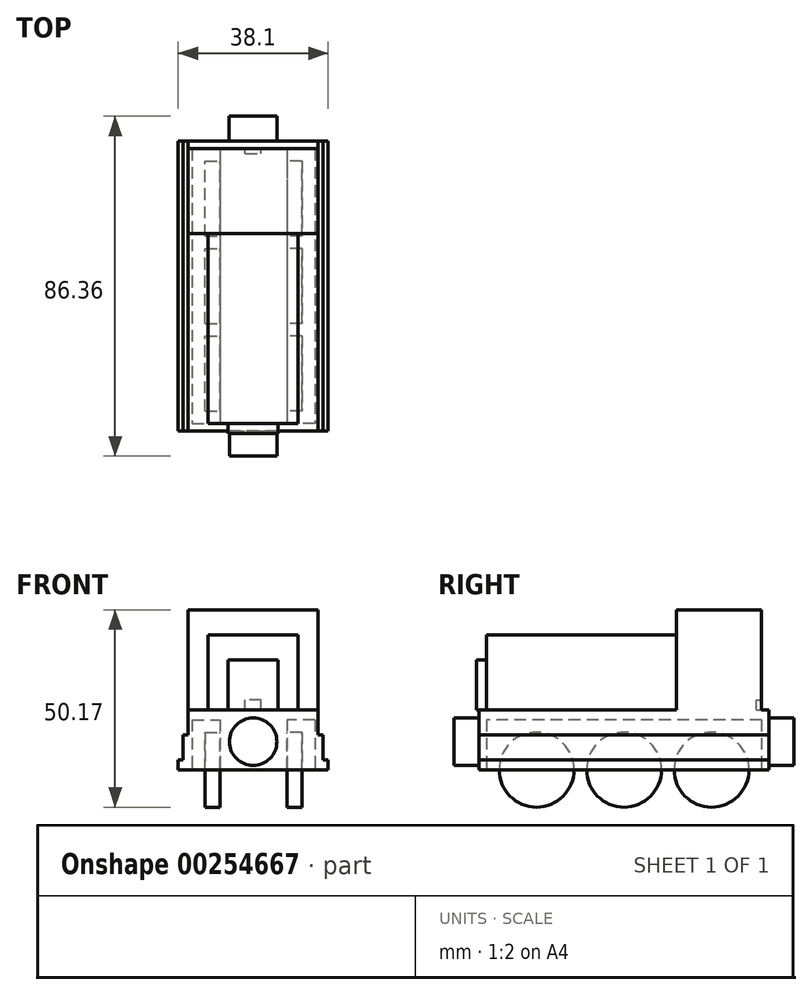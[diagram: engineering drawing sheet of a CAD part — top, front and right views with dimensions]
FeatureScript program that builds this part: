
annotation { "Feature Type Name" : "Feature", "Feature Type Description" : "" }
export const myFeature = defineFeature(function(context is Context, id is Id, definition is map)
    precondition{}
    {
        {
            var Q0;
            Q0=qCreatedBy(makeId("Front.planeOp"),FACE);
            var sketch = newSketch(context, id + "F0", { "sketchPlane" : qUnion([Q0])});
            skLineSegment(sketch, "E0.bottom", {"start": v(-16.51, 12.7) * mm, "end": v(16.51, 12.7) * mm});
            skLineSegment(sketch, "E0.top", {"start": v(-16.51, -12.7) * mm, "end": v(16.51, -12.7) * mm});
            skLineSegment(sketch, "E0.left", {"start": v(-16.51, 12.7) * mm, "end": v(-16.51, -12.7) * mm});
            skLineSegment(sketch, "E0.right", {"start": v(16.51, 12.7) * mm, "end": v(16.51, -12.7) * mm});
            skPoint(sketch, "E0.middle", {"position": v(0, 0) * mm});
            skSolve(sketch);
        }
        {
            var Q0;
            Q0 = qSketchRegion(id + "F0", true);
            extrude(context, id + "F1", {"entities" : qUnion([Q0]), "endBound" : BoundingType.SYMMETRIC, "depth" : 21.59 * mm});
        }
        {
            var Q0;
            Q0=makeQuery(id+"F1.opExtrude","CAP_FACE",FACE,{"disambiguationData":[OSD([sQuery(id+"F0.wireOp",EDGE,"E0.bottom"),sQuery(id+"F0.wireOp",EDGE,"E0.top"),sQuery(id+"F0.wireOp",EDGE,"E0.left"),sQuery(id+"F0.wireOp",EDGE,"E0.right")])],"isStart":false});
            var sketch = newSketch(context, id + "F2", { "sketchPlane" : qUnion([Q0])});
            skLineSegment(sketch, "E1.bottom", {"start": v(-11.43, 6.35) * mm, "end": v(11.43, 6.35) * mm});
            skLineSegment(sketch, "E1.top", {"start": v(-11.43, -12.7) * mm, "end": v(11.43, -12.7) * mm});
            skLineSegment(sketch, "E1.left", {"start": v(-11.43, 6.35) * mm, "end": v(-11.43, -12.7) * mm});
            skLineSegment(sketch, "E1.right", {"start": v(11.43, 6.35) * mm, "end": v(11.43, -12.7) * mm});
            skPoint(sketch, "E2", {"position": v(0, -12.7) * mm});
            skPoint(sketch, "E3", {"position": v(67.06, 31.88) * mm});
            skSolve(sketch);
        }
        {
            var Q0;
            Q0 = qSketchRegion(id + "F2", true);
            extrude(context, id + "F3", {"entities" : qUnion([Q0]), "operationType" : NewBodyOperationType.ADD, "depth" : 48.26 * mm});
        }
        {
            var Q0;
            Q0=qCreatedBy(makeId("Front.planeOp"),FACE);
            var sketch = newSketch(context, id + "F4", { "sketchPlane" : qUnion([Q0])});
            skLineSegment(sketch, "E4.bottom", {"start": v(-16.5, -12.7) * mm, "end": v(16.51, -12.7) * mm});
            skLineSegment(sketch, "E4.top", {"start": v(-16.5, -27.94) * mm, "end": v(16.51, -27.94) * mm});
            skLineSegment(sketch, "E4.left", {"start": v(-16.5, -12.7) * mm, "end": v(-16.5, -27.94) * mm});
            skLineSegment(sketch, "E4.right", {"start": v(16.51, -12.7) * mm, "end": v(16.51, -27.94) * mm});
            skSolve(sketch);
        }
        {
            var Q0;
            Q0=makeQuery(id+"F4.imprint","IMPRINT",FACE,{"disambiguationData":[TD([[makeQuery(id+"F4.imprint","IMPRINT",EDGE,{"derivedFrom":sQuery(id+"F4.wireOp",EDGE,"E4.bottom")}),-1.0]])]});
            extrude(context, id + "F5", {"entities" : qUnion([Q0]), "operationType" : NewBodyOperationType.ADD, "endBound" : BoundingType.SYMMETRIC, "depth" : 25.4 * mm});
        }
        {
            var Q0;
            Q0=makeQuery(id+"F5.opExtrude","CAP_FACE",FACE,{"disambiguationData":[OSD([sQuery(id+"F4.wireOp",EDGE,"E4.bottom"),sQuery(id+"F4.wireOp",EDGE,"E4.top"),sQuery(id+"F4.wireOp",EDGE,"E4.left"),sQuery(id+"F4.wireOp",EDGE,"E4.right")])],"isStart":false});
            var sketch = newSketch(context, id + "F6", { "sketchPlane" : qUnion([Q0])});
            skLineSegment(sketch, "E5.bottom", {"start": v(-16.5, -12.7) * mm, "end": v(16.51, -12.7) * mm});
            skLineSegment(sketch, "E5.top", {"start": v(-16.5, -27.94) * mm, "end": v(16.51, -27.94) * mm});
            skLineSegment(sketch, "E5.left", {"start": v(-16.5, -12.7) * mm, "end": v(-16.5, -27.94) * mm});
            skLineSegment(sketch, "E5.right", {"start": v(16.51, -12.7) * mm, "end": v(16.51, -27.94) * mm});
            skSolve(sketch);
        }
        {
            var Q0;
            Q0 = qSketchRegion(id + "F6", true);
            extrude(context, id + "F7", {"entities" : qUnion([Q0]), "operationType" : NewBodyOperationType.ADD, "depth" : 48.26 * mm});
        }
        {
            var Q0;
            Q0=makeQuery(id+"F3.opExtrude","CAP_FACE",FACE,{"disambiguationData":[OSD([sQuery(id+"F2.wireOp",EDGE,"E1.bottom"),sQuery(id+"F2.wireOp",EDGE,"E1.top"),sQuery(id+"F2.wireOp",EDGE,"E1.left"),sQuery(id+"F2.wireOp",EDGE,"E1.right")])],"isStart":false});
            var sketch = newSketch(context, id + "F8", { "sketchPlane" : qUnion([Q0])});
            skLineSegment(sketch, "E6.bottom", {"start": v(-6.35, 0) * mm, "end": v(6.35, 0) * mm});
            skLineSegment(sketch, "E6.top", {"start": v(-6.35, -12.7) * mm, "end": v(6.35, -12.7) * mm});
            skLineSegment(sketch, "E6.left", {"start": v(-6.35, 0) * mm, "end": v(-6.35, -12.7) * mm});
            skLineSegment(sketch, "E6.right", {"start": v(6.35, 0) * mm, "end": v(6.35, -12.7) * mm});
            skPoint(sketch, "E6.middle", {"position": v(0, -6.35) * mm});
            skSolve(sketch);
        }
        {
            var Q0;
            Q0 = qSketchRegion(id + "F8", true);
            extrude(context, id + "F9", {"entities" : qUnion([Q0]), "operationType" : NewBodyOperationType.ADD, "depth" : 2.54 * mm});
        }
        {
            var Q0;
            Q0=makeQuery(id+"F7.boolean.opBoolean","MERGE",FACE,{"derivedFrom":[makeQuery(id+"F5.opExtrude","SWEPT_FACE",FACE,{"disambiguationData":[OSD([sQuery(id+"F4.wireOp",EDGE,"E4.top")])]}),makeQuery(id+"F7.opExtrude","SWEPT_FACE",FACE,{"disambiguationData":[OSD([sQuery(id+"F6.wireOp",EDGE,"E5.top")])]})]});
            var sketch = newSketch(context, id + "F10", { "sketchPlane" : qUnion([Q0])});
            skLineSegment(sketch, "E7.bottom", {"start": v(-15.5, -10.8) * mm, "end": v(-8.38, -10.8) * mm});
            skLineSegment(sketch, "E7.top", {"start": v(-15.5, 59.05) * mm, "end": v(-8.38, 59.05) * mm});
            skLineSegment(sketch, "E7.left", {"start": v(-15.5, -10.8) * mm, "end": v(-15.5, 59.06) * mm});
            skLineSegment(sketch, "E7.right", {"start": v(-8.38, -10.8) * mm, "end": v(-8.38, 59.05) * mm});
            skLineSegment(sketch, "E8.bottom", {"start": v(15.67, -10.8) * mm, "end": v(8.56, -10.8) * mm});
            skLineSegment(sketch, "E8.top", {"start": v(15.67, 59.05) * mm, "end": v(8.56, 59.05) * mm});
            skLineSegment(sketch, "E8.left", {"start": v(15.67, -10.8) * mm, "end": v(15.67, 59.05) * mm});
            skLineSegment(sketch, "E8.right", {"start": v(8.56, -10.8) * mm, "end": v(8.56, 59.05) * mm});
            skPoint(sketch, "E9", {"position": v(15.67, 24.13) * mm});
            skPoint(sketch, "E9.positionSnap0", {"position": v(-16.5, 24.13) * mm});
            skSolve(sketch);
        }
        {
            var Q0;
            Q0 = qSketchRegion(id + "F10", true);
            extrude(context, id + "F11", {"entities" : qUnion([Q0]), "operationType" : NewBodyOperationType.REMOVE, "oppositeDirection" : true, "depth" : 12.7 * mm});
        }
        {
            var Q0;
            Q0=makeQuery(id+"F11.boolean.opBoolean","COPY",FACE,{"derivedFrom":makeQuery(id+"F11.opExtrude","SWEPT_FACE",FACE,{"disambiguationData":[OSD([sQuery(id+"F10.wireOp",EDGE,"E7.right")])]})});
            var sketch = newSketch(context, id + "F12", { "sketchPlane" : qUnion([Q0])});
            skPoint(sketch, "E10", {"position": v(24.13, -27.94) * mm});
            skCircle(sketch, "E11", {"center": v(24.13, -27.94) * mm, "radius": 9.53 * mm});
            skSolve(sketch);
        }
        {
            var Q0;
            Q0=makeQuery(id+"F7.opExtrude","CAP_FACE",FACE,{"disambiguationData":[OSD([sQuery(id+"F6.wireOp",EDGE,"E5.bottom"),sQuery(id+"F6.wireOp",EDGE,"E5.top"),sQuery(id+"F6.wireOp",EDGE,"E5.left"),sQuery(id+"F6.wireOp",EDGE,"E5.right")])],"isStart":false});
            var sketch = newSketch(context, id + "F13", { "sketchPlane" : qUnion([Q0])});
            skCircle(sketch, "E12", {"center": v(0, -20.81) * mm, "radius": 6.03 * mm});
            skSolve(sketch);
        }
        {
            var Q0;
            Q0 = qSketchRegion(id + "F13", true);
            extrude(context, id + "F14", {"entities" : qUnion([Q0]), "operationType" : NewBodyOperationType.ADD, "depth" : 6.35 * mm});
        }
        {
            var Q0;
            Q0 = qSketchRegion(id + "F12", true);
            extrude(context, id + "F15", {"entities" : qUnion([Q0]), "operationType" : NewBodyOperationType.ADD, "depth" : 3.8 * mm});
        }
        {
            var Q0;
            Q0=makeQuery(id+"F11.boolean.opBoolean","COPY",FACE,{"derivedFrom":makeQuery(id+"F11.opExtrude","SWEPT_FACE",FACE,{"disambiguationData":[OSD([sQuery(id+"F10.wireOp",EDGE,"E7.right")])]})});
            var sketch = newSketch(context, id + "F16", { "sketchPlane" : qUnion([Q0])});
            skPoint(sketch, "E13", {"position": v(46.35, -27.94) * mm});
            skCircle(sketch, "E14", {"center": v(46.35, -27.94) * mm, "radius": 9.53 * mm});
            skSolve(sketch);
        }
        {
            var Q0;
            Q0 = qSketchRegion(id + "F16", true);
            extrude(context, id + "F17", {"entities" : qUnion([Q0]), "operationType" : NewBodyOperationType.ADD, "depth" : 3.8 * mm});
        }
        {
            var Q0;
            Q0=makeQuery(id+"F11.boolean.opBoolean","COPY",FACE,{"derivedFrom":makeQuery(id+"F11.opExtrude","SWEPT_FACE",FACE,{"disambiguationData":[OSD([sQuery(id+"F10.wireOp",EDGE,"E7.right")])]})});
            var sketch = newSketch(context, id + "F18", { "sketchPlane" : qUnion([Q0])});
            skPoint(sketch, "E15", {"position": v(1.9, -27.94) * mm});
            skCircle(sketch, "E16", {"center": v(1.9, -27.94) * mm, "radius": 9.53 * mm});
            skSolve(sketch);
        }
        {
            var Q0;
            Q0 = qSketchRegion(id + "F18", true);
            extrude(context, id + "F19", {"entities" : qUnion([Q0]), "operationType" : NewBodyOperationType.ADD, "depth" : 3.8 * mm});
        }
        {
            var Q0;
            Q0=makeQuery(id+"F11.boolean.opBoolean","COPY",FACE,{"derivedFrom":makeQuery(id+"F11.opExtrude","SWEPT_FACE",FACE,{"disambiguationData":[OSD([sQuery(id+"F10.wireOp",EDGE,"E8.right")])]})});
            var sketch = newSketch(context, id + "F20", { "sketchPlane" : qUnion([Q0])});
            skPoint(sketch, "E17", {"position": v(-24.13, -27.94) * mm});
            skCircle(sketch, "E18", {"center": v(-24.13, -27.94) * mm, "radius": 9.53 * mm});
            skSolve(sketch);
        }
        {
            var Q0;
            Q0 = qSketchRegion(id + "F20", true);
            extrude(context, id + "F21", {"entities" : qUnion([Q0]), "operationType" : NewBodyOperationType.ADD, "depth" : 3.8 * mm});
        }
        {
            var Q0;
            Q0=makeQuery(id+"F11.boolean.opBoolean","COPY",FACE,{"derivedFrom":makeQuery(id+"F11.opExtrude","SWEPT_FACE",FACE,{"disambiguationData":[OSD([sQuery(id+"F10.wireOp",EDGE,"E8.right")])]})});
            var sketch = newSketch(context, id + "F22", { "sketchPlane" : qUnion([Q0])});
            skCircle(sketch, "E19", {"center": v(-1.9, -27.94) * mm, "radius": 9.53 * mm});
            skSolve(sketch);
        }
        {
            var Q0;
            Q0 = qSketchRegion(id + "F22", true);
            extrude(context, id + "F23", {"entities" : qUnion([Q0]), "operationType" : NewBodyOperationType.ADD, "depth" : 3.8 * mm});
        }
        {
            var Q0;
            Q0=makeQuery(id+"F11.boolean.opBoolean","COPY",FACE,{"derivedFrom":makeQuery(id+"F11.opExtrude","SWEPT_FACE",FACE,{"disambiguationData":[OSD([sQuery(id+"F10.wireOp",EDGE,"E8.right")])]})});
            var sketch = newSketch(context, id + "F24", { "sketchPlane" : qUnion([Q0])});
            skPoint(sketch, "E20", {"position": v(-46.35, -27.94) * mm});
            skCircle(sketch, "E21", {"center": v(-46.35, -27.94) * mm, "radius": 9.53 * mm});
            skSolve(sketch);
        }
        {
            var Q0;
            Q0 = qSketchRegion(id + "F24", true);
            extrude(context, id + "F25", {"entities" : qUnion([Q0]), "operationType" : NewBodyOperationType.ADD, "depth" : 3.8 * mm});
        }
        {
            var Q0;
            Q0=makeQuery(id+"F5.opExtrude","CAP_FACE",FACE,{"disambiguationData":[OSD([sQuery(id+"F4.wireOp",EDGE,"E4.bottom"),sQuery(id+"F4.wireOp",EDGE,"E4.top"),sQuery(id+"F4.wireOp",EDGE,"E4.left"),sQuery(id+"F4.wireOp",EDGE,"E4.right")])],"isStart":true});
            var sketch = newSketch(context, id + "F26", { "sketchPlane" : qUnion([Q0])});
            skPoint(sketch, "E22.centerSnap0", {"position": v(0, -27.94) * mm});
            skCircle(sketch, "E23", {"center": v(0.01, -20.82) * mm, "radius": 6.07 * mm});
            skPoint(sketch, "E23.first.point", {"position": v(-4.4, -25) * mm});
            skPoint(sketch, "E23.second.point", {"position": v(4.4, -16.63) * mm});
            skPoint(sketch, "E23.third.point", {"position": v(5.44, -23.53) * mm});
            skSolve(sketch);
        }
        {
            var Q0;
            Q0 = qSketchRegion(id + "F26", true);
            extrude(context, id + "F27", {"entities" : qUnion([Q0]), "operationType" : NewBodyOperationType.ADD, "depth" : 6.35 * mm});
        }
        {
            var Q0;
            Q0=makeQuery(id+"F7.boolean.opBoolean","MERGE",FACE,{"derivedFrom":[makeQuery(id+"F5.boolean.opBoolean","MERGE",FACE,{"derivedFrom":[makeQuery(id+"F1.opExtrude","SWEPT_FACE",FACE,{"disambiguationData":[OSD([sQuery(id+"F0.wireOp",EDGE,"E0.right")])]}),makeQuery(id+"F5.opExtrude","SWEPT_FACE",FACE,{"disambiguationData":[OSD([sQuery(id+"F4.wireOp",EDGE,"E4.right")])]})]}),makeQuery(id+"F7.opExtrude","SWEPT_FACE",FACE,{"disambiguationData":[OSD([sQuery(id+"F6.wireOp",EDGE,"E5.right")])]})]});
            var sketch = newSketch(context, id + "F28", { "sketchPlane" : qUnion([Q0])});
            skLineSegment(sketch, "E24.bottom", {"start": v(-60.96, -19.05) * mm, "end": v(12.7, -19.05) * mm});
            skLineSegment(sketch, "E24.top", {"start": v(-60.96, -27.94) * mm, "end": v(12.7, -27.94) * mm});
            skLineSegment(sketch, "E24.left", {"start": v(-60.96, -19.05) * mm, "end": v(-60.96, -27.94) * mm});
            skLineSegment(sketch, "E24.right", {"start": v(12.7, -19.05) * mm, "end": v(12.7, -27.94) * mm});
            skSolve(sketch);
        }
        {
            var Q0;
            Q0 = qSketchRegion(id + "F28", true);
            extrude(context, id + "F29", {"entities" : qUnion([Q0]), "operationType" : NewBodyOperationType.ADD, "depth" : 1.27 * mm});
        }
        {
            var Q0;
            Q0=makeQuery(id+"F7.boolean.opBoolean","MERGE",FACE,{"derivedFrom":[makeQuery(id+"F5.boolean.opBoolean","MERGE",FACE,{"derivedFrom":[makeQuery(id+"F1.opExtrude","SWEPT_FACE",FACE,{"disambiguationData":[OSD([sQuery(id+"F0.wireOp",EDGE,"E0.left")])]}),makeQuery(id+"F5.opExtrude","SWEPT_FACE",FACE,{"disambiguationData":[OSD([sQuery(id+"F4.wireOp",EDGE,"E4.left")])]})]}),makeQuery(id+"F7.opExtrude","SWEPT_FACE",FACE,{"disambiguationData":[OSD([sQuery(id+"F6.wireOp",EDGE,"E5.left")])]})]});
            var sketch = newSketch(context, id + "F30", { "sketchPlane" : qUnion([Q0])});
            skLineSegment(sketch, "E25.bottom", {"start": v(-12.7, -27.94) * mm, "end": v(60.96, -27.94) * mm});
            skLineSegment(sketch, "E25.top", {"start": v(-12.7, -19.05) * mm, "end": v(60.96, -19.05) * mm});
            skLineSegment(sketch, "E25.left", {"start": v(-12.7, -27.94) * mm, "end": v(-12.7, -19.05) * mm});
            skLineSegment(sketch, "E25.right", {"start": v(60.96, -27.94) * mm, "end": v(60.96, -19.05) * mm});
            skSolve(sketch);
        }
        {
            var Q0;
            Q0 = qSketchRegion(id + "F30", true);
            extrude(context, id + "F31", {"entities" : qUnion([Q0]), "operationType" : NewBodyOperationType.ADD, "depth" : 1.27 * mm});
        }
        {
            var Q0;
            Q0=makeQuery(id+"F29.opExtrude","CAP_FACE",FACE,{"disambiguationData":[OSD([sQuery(id+"F28.wireOp",EDGE,"E24.bottom"),sQuery(id+"F28.wireOp",EDGE,"E24.top"),sQuery(id+"F28.wireOp",EDGE,"E24.left"),sQuery(id+"F28.wireOp",EDGE,"E24.right")])],"isStart":false});
            var sketch = newSketch(context, id + "F32", { "sketchPlane" : qUnion([Q0])});
            skLineSegment(sketch, "E26.bottom", {"start": v(-60.96, -27.94) * mm, "end": v(12.7, -27.94) * mm});
            skLineSegment(sketch, "E26.top", {"start": v(-60.96, -25.4) * mm, "end": v(12.7, -25.4) * mm});
            skLineSegment(sketch, "E26.left", {"start": v(-60.96, -27.94) * mm, "end": v(-60.96, -25.4) * mm});
            skLineSegment(sketch, "E26.right", {"start": v(12.7, -27.94) * mm, "end": v(12.7, -25.4) * mm});
            skSolve(sketch);
        }
        {
            var Q0;
            Q0 = qSketchRegion(id + "F32", true);
            extrude(context, id + "F33", {"entities" : qUnion([Q0]), "operationType" : NewBodyOperationType.ADD, "depth" : 1.27 * mm});
        }
        {
            var Q0;
            Q0=makeQuery(id+"F31.opExtrude","CAP_FACE",FACE,{"disambiguationData":[OSD([sQuery(id+"F30.wireOp",EDGE,"E25.bottom"),sQuery(id+"F30.wireOp",EDGE,"E25.top"),sQuery(id+"F30.wireOp",EDGE,"E25.left"),sQuery(id+"F30.wireOp",EDGE,"E25.right")])],"isStart":false});
            var sketch = newSketch(context, id + "F34", { "sketchPlane" : qUnion([Q0])});
            skLineSegment(sketch, "E27.bottom", {"start": v(-12.7, -27.94) * mm, "end": v(60.96, -27.94) * mm});
            skLineSegment(sketch, "E27.top", {"start": v(-12.7, -25.4) * mm, "end": v(60.96, -25.4) * mm});
            skLineSegment(sketch, "E27.left", {"start": v(-12.7, -27.94) * mm, "end": v(-12.7, -25.4) * mm});
            skLineSegment(sketch, "E27.right", {"start": v(60.96, -27.94) * mm, "end": v(60.96, -25.4) * mm});
            skSolve(sketch);
        }
        {
            var Q0;
            Q0 = qSketchRegion(id + "F34", true);
            extrude(context, id + "F35", {"entities" : qUnion([Q0]), "operationType" : NewBodyOperationType.ADD, "depth" : 1.27 * mm});
        }
        {
            var Q0;
            Q0=makeQuery(id+"F1.opExtrude","CAP_FACE",FACE,{"disambiguationData":[OSD([sQuery(id+"F0.wireOp",EDGE,"E0.bottom"),sQuery(id+"F0.wireOp",EDGE,"E0.top"),sQuery(id+"F0.wireOp",EDGE,"E0.left"),sQuery(id+"F0.wireOp",EDGE,"E0.right")])],"isStart":true});
            var sketch = newSketch(context, id + "F36", { "sketchPlane" : qUnion([Q0])});
            skLineSegment(sketch, "E28.bottom", {"start": v(-2.05, -12.7) * mm, "end": v(2.02, -12.7) * mm});
            skLineSegment(sketch, "E28.top", {"start": v(-2.05, -10.16) * mm, "end": v(2.02, -10.16) * mm});
            skLineSegment(sketch, "E28.left", {"start": v(-2.05, -12.7) * mm, "end": v(-2.05, -10.16) * mm});
            skLineSegment(sketch, "E28.right", {"start": v(2.02, -12.7) * mm, "end": v(2.02, -10.16) * mm});
            skSolve(sketch);
        }
        {
            var Q0;
            Q0 = qSketchRegion(id + "F36", true);
            extrude(context, id + "F37", {"entities" : qUnion([Q0]), "operationType" : NewBodyOperationType.REMOVE, "oppositeDirection" : true, "depth" : 1.27 * mm});
        }
    });
